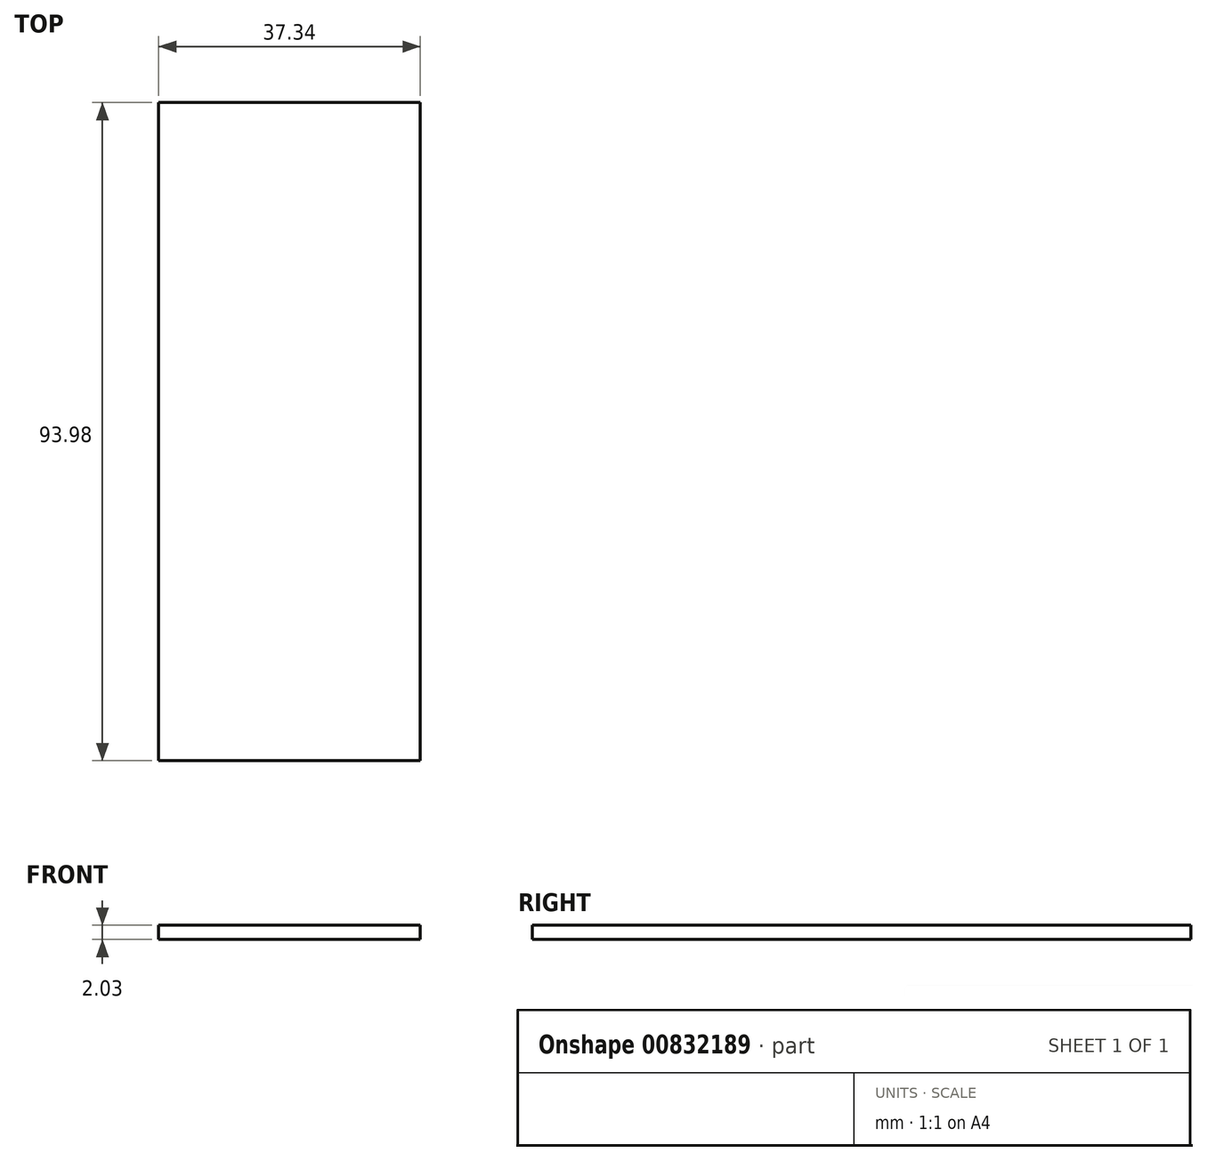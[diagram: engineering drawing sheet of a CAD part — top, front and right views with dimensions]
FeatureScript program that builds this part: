
annotation { "Feature Type Name" : "Feature", "Feature Type Description" : "" }
export const myFeature = defineFeature(function(context is Context, id is Id, definition is map)
    precondition{}
    {
        {
            var Q0;
            Q0=qCreatedBy(makeId("Top.planeOp"),FACE);
            var sketch = newSketch(context, id + "F0", { "sketchPlane" : qUnion([Q0])});
            skLineSegment(sketch, "E0.bottom", {"start": v(-18.67, 47) * mm, "end": v(18.67, 47) * mm});
            skLineSegment(sketch, "E0.top", {"start": v(-18.67, -47) * mm, "end": v(18.67, -47) * mm});
            skLineSegment(sketch, "E0.left", {"start": v(-18.67, 47) * mm, "end": v(-18.67, -47) * mm});
            skLineSegment(sketch, "E0.right", {"start": v(18.67, 47) * mm, "end": v(18.67, -47) * mm});
            skPoint(sketch, "E0.middle", {"position": v(0, 0) * mm});
            skSolve(sketch);
        }
        {
            var Q0;
            Q0=makeQuery(id+"F0.imprint","IMPRINT",FACE,{"disambiguationData":[TD([[makeQuery(id+"F0.imprint","IMPRINT",EDGE,{"derivedFrom":sQuery(id+"F0.wireOp",EDGE,"E0.bottom")}),-1.0]])]});
            extrude(context, id + "F1", {"entities" : qUnion([Q0]), "depth" : 2.03 * mm, "offsetDistance" : 25.4 * mm});
        }
    });
